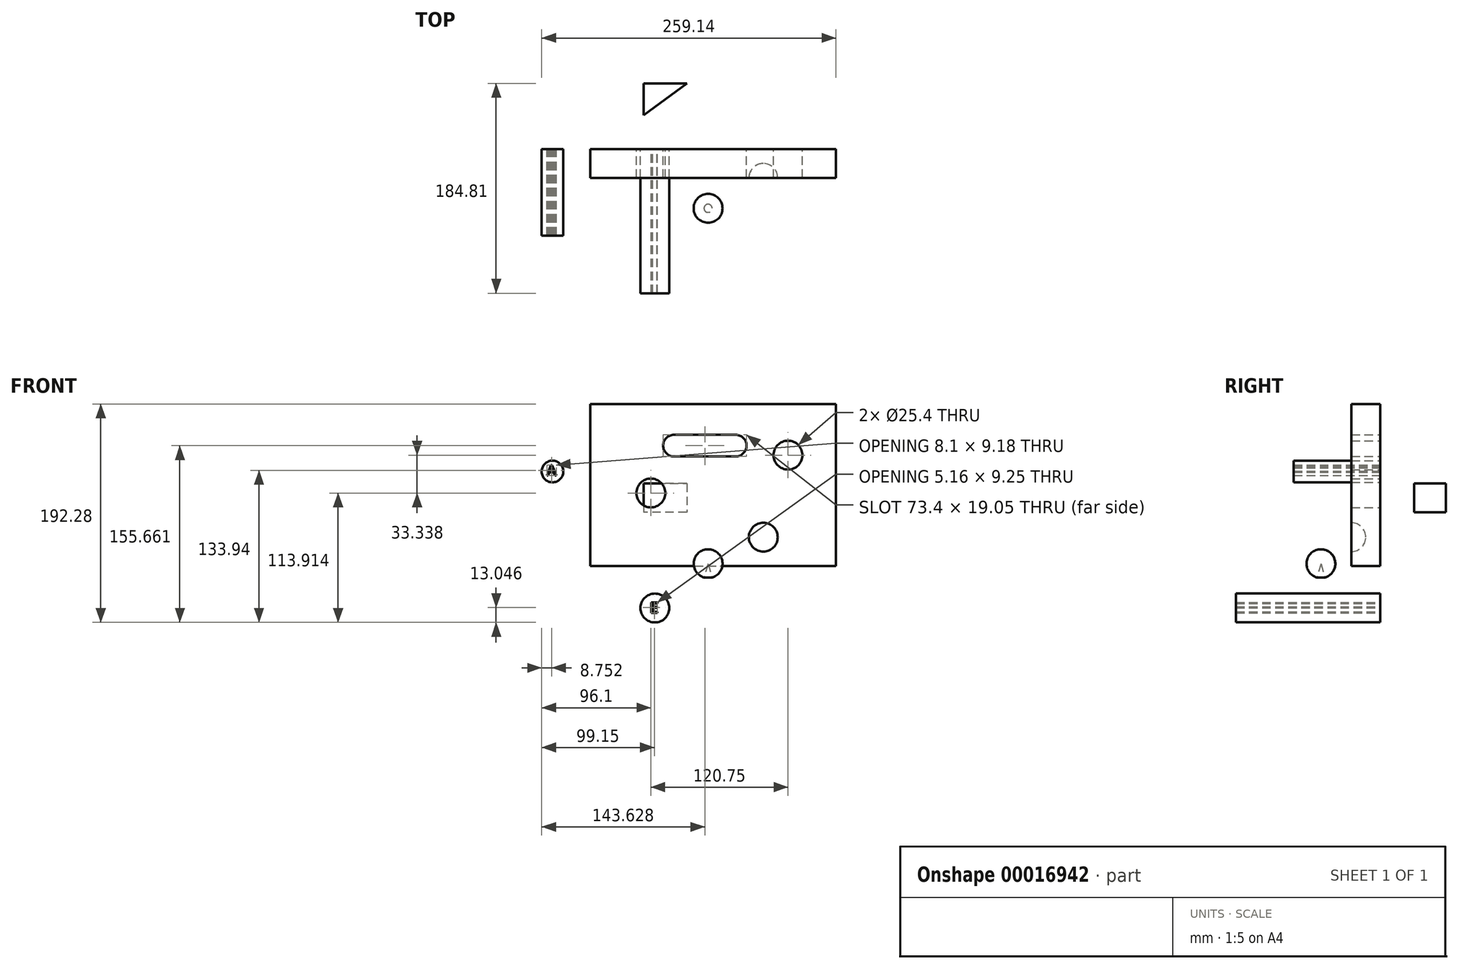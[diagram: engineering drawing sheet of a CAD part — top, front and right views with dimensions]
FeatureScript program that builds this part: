
annotation { "Feature Type Name" : "Feature", "Feature Type Description" : "" }
export const myFeature = defineFeature(function(context is Context, id is Id, definition is map)
    precondition{}
    {
        {
            var Q0;
            Q0=qCreatedBy(makeId("Front.planeOp"),FACE);
            var sketch = newSketch(context, id + "F0", { "sketchPlane" : qUnion([Q0])});
            skLineSegment(sketch, "E0.bottom", {"start": v(-103.8, 95.4) * mm, "end": v(112.64, 95.4) * mm});
            skLineSegment(sketch, "E0.top", {"start": v(-103.8, -47.24) * mm, "end": v(112.64, -47.24) * mm});
            skLineSegment(sketch, "E0.left", {"start": v(-103.8, 95.4) * mm, "end": v(-103.8, -47.24) * mm});
            skLineSegment(sketch, "E0.right", {"start": v(112.64, 95.4) * mm, "end": v(112.64, -47.24) * mm});
            skCircle(sketch, "E1", {"center": v(-50.4, 17.04) * mm, "radius": 12.7 * mm});
            skLineSegment(sketch, "E2", {"start": v(-30.05, 68.32) * mm, "end": v(24.3, 68.32) * mm});
            skLineSegment(sketch, "E3", {"start": v(-30.05, 49.27) * mm, "end": v(24.3, 49.27) * mm});
            skArc(sketch, "E4", {"start": v(-30.05, 68.32) * mm, "mid": v(-39.57, 58.8) * mm, "end": v(-30.05, 49.27) * mm});
            skArc(sketch, "E5", {"start": v(24.3, 68.32) * mm, "mid": v(33.83, 58.8) * mm, "end": v(24.3, 49.27) * mm});
            skCircle(sketch, "E6", {"center": v(70.35, 50.38) * mm, "radius": 12.7 * mm});
            skSolve(sketch);
        }
        {
            var Q0;
            Q0=makeQuery(id+"F0.imprint","IMPRINT",FACE,{"disambiguationData":[TD([[makeQuery(id+"F0.imprint","IMPRINT",EDGE,{"derivedFrom":sQuery(id+"F0.wireOp",EDGE,"E0.bottom")}),-1.0]])]});
            extrude(context, id + "F1", {"entities" : qUnion([Q0]), "depth" : 25.4 * mm});
        }
        {
            var Q0;
            Q0=qCreatedBy(makeId("Front.planeOp"),FACE);
            var sketch = newSketch(context, id + "F2", { "sketchPlane" : qUnion([Q0])});
            skCircle(sketch, "E7", {"center": v(-46.84, -84.17) * mm, "radius": 12.7 * mm});
            skText(sketch, "E8", { "text": "E", "fontName": "OpenSans-Regular.ttf"});
            const initialGuessF2  = {"E8": [-0.0512, -0.08845, 1, 0, 0.00933]};
            skSetInitialGuess(sketch, initialGuessF2);
            skSolve(sketch);
        }
        {
            var Q0;
            Q0=makeQuery(id+"F2.imprint","IMPRINT",FACE,{"disambiguationData":[TD([[makeQuery(id+"F2.imprint","IMPRINT",EDGE,{"derivedFrom":sQuery(id+"F2.wireOp",EDGE,"E7")}),1.0]])]});
            extrude(context, id + "F3", {"entities" : qUnion([Q0]), "depth" : 127 * mm});
        }
        {
            var Q0;
            Q0=qCreatedBy(makeId("Front.planeOp"),FACE);
            var sketch = newSketch(context, id + "F4", { "sketchPlane" : qUnion([Q0])});
            skCircle(sketch, "E9", {"center": v(-136.97, 36.01) * mm, "radius": 9.53 * mm});
            skText(sketch, "E10", { "text": "A", "fontName": "OpenSans-Regular.ttf"});
            const initialGuessF4  = {"E10": [-0.1418, 0.03248, 1, 0, 0.00922]};
            skSetInitialGuess(sketch, initialGuessF4);
            skSolve(sketch);
        }
        {
            var Q0;
            Q0=makeQuery(id+"F4.imprint","IMPRINT",FACE,{"disambiguationData":[TD([[makeQuery(id+"F4.imprint","IMPRINT",EDGE,{"derivedFrom":sQuery(id+"F4.wireOp",EDGE,"E9")}),1.0]])]});
            var Q1;
            Q1=makeQuery(id+"F4.imprint","IMPRINT",FACE,{"disambiguationData":[TD([[makeQuery(id+"F4.imprint","IMPRINT",EDGE,{"derivedFrom":sQuery(id+"F4.wireOp",EDGE,"E10.sketch_text.stroke-8")}),1.0]])]});
            extrude(context, id + "F5", {"entities" : qUnion([Q0, Q1]), "depth" : 76.2 * mm});
        }
        {
            var Q0;
            Q0=qCreatedBy(makeId("Top.planeOp"),FACE);
            var sketch = newSketch(context, id + "F6", { "sketchPlane" : qUnion([Q0])});
            skLineSegment(sketch, "E11", {"start": v(-56.64, 29.73) * mm, "end": v(-56.64, 57.81) * mm});
            skLineSegment(sketch, "E12", {"start": v(-56.64, 57.81) * mm, "end": v(-18.72, 57.81) * mm});
            skLineSegment(sketch, "E13", {"start": v(-18.72, 57.81) * mm, "end": v(-56.64, 29.73) * mm});
            skSolve(sketch);
        }
        {
            var Q0;
            Q0=makeQuery(id+"F6.imprint","IMPRINT",FACE,{"disambiguationData":[TD([[makeQuery(id+"F6.imprint","IMPRINT",EDGE,{"derivedFrom":sQuery(id+"F6.wireOp",EDGE,"E11")}),-1.0]])]});
            extrude(context, id + "F7", {"entities" : qUnion([Q0]), "depth" : 25.4 * mm});
        }
        {
            var Q0;
            Q0=makeQuery(id+"F1.opExtrude","SWEPT_FACE",FACE,{"disambiguationData":[OSD([sQuery(id+"F0.wireOp",EDGE,"E0.top")])]});
            cPlane(context, id + "F8", {"entities" : qUnion([Q0]), "cplaneType" : CPlaneType.OFFSET, "offset" : 25.4 * mm, "oppositeDirection" : true, "width" : 152.4 * mm, "height" : 152.4 * mm});
        }
        {
            var Q0;
            Q0=qCreatedBy(id+"F8.planeOp",FACE);
            var sketch = newSketch(context, id + "F9", { "sketchPlane" : qUnion([Q0])});
            skLineSegment(sketch, "E14.0", {"start": v(-103.8, 25.4) * mm, "end": v(112.64, 25.4) * mm, "construction": true});
            skArc(sketch, "E15", {"start": v(35.88, 25.4) * mm, "mid": v(39.6, 16.42) * mm, "end": v(48.58, 12.7) * mm});
            skLineSegment(sketch, "E16", {"start": v(35.88, 25.4) * mm, "end": v(48.58, 25.4) * mm});
            skLineSegment(sketch, "E17", {"start": v(48.58, 12.7) * mm, "end": v(48.58, 25.4) * mm});
            skSolve(sketch);
        }
        {
            var Q0;
            Q0 = qSketchRegion(id + "F9", true);
            var Q1;
            Q1=sQuery(id+"F9.wireOp",EDGE,"E17");
            revolve(context, id + "F10", {"operationType" : NewBodyOperationType.REMOVE, "entities" : qUnion([Q0]), "axis" : qUnion([Q1]), "revolveType" : RevolveType.FULL, "oppositeDirection" : true});
        }
        {
            var Q0;
            Q0=qCreatedBy(makeId("Right.planeOp"),FACE);
            var sketch = newSketch(context, id + "F11", { "sketchPlane" : qUnion([Q0])});
            skLineSegment(sketch, "E18", {"start": v(-52.23, -32.47) * mm, "end": v(-52.23, -57.87) * mm});
            skArc(sketch, "E19", {"start": v(-52.23, -57.87) * mm, "mid": v(-39.53, -45.17) * mm, "end": v(-52.23, -32.47) * mm});
            skLineSegment(sketch, "E20", {"start": v(-52.23, -45.17) * mm, "end": v(-48.65, -57.36) * mm});
            skSolve(sketch);
        }
        {
            var Q0;
            {var subQ0=sQuery(id+"F11.wireOp",EDGE,"E20");Q0=makeQuery(id+"F11.imprint","IMPRINT",FACE,{"disambiguationData":[TD([[makeQuery(id+"F11.imprint","IMPRINT",EDGE,{"derivedFrom":subQ0}),1.0]])]});}
            var Q1;
            Q1=sQuery(id+"F11.wireOp",EDGE,"E18");
            revolve(context, id + "F12", {"operationType" : NewBodyOperationType.ADD, "entities" : qUnion([Q0]), "axis" : qUnion([Q1]), "revolveType" : RevolveType.FULL});
        }
    });
